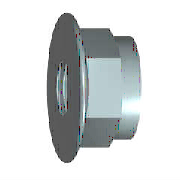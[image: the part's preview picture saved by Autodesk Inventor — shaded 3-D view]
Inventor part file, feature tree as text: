
AUTODESK INVENTOR PART (.ipt)
format: ipt  version: 2018 (Build 220112000, 112)  size: 212,480 bytes
history: native  units: mm (DEFAULTED — no unit token found)
features: other x3, sketch x3, extrude x2, hole x1, plane x1
ambient origin geometry x7: Origin, YZ Plane, XZ Plane, X Axis, Y Axis, Z Axis, Center Point
bodies: Solid1 (feature_tree)
feature tree (10):
  other  "Anello"
  extrude  "Corpo"  Depth=34.5mm
  extrude  "Corona"  Depth=2.4mm
  hole  "Filettatura"  [1 undecoded]
  other  "Smusso1"
  other  "Work Axis1"
  plane  "Work Plane1"
  sketch  "Schizzo1"
  sketch  "Schizzo5"
  sketch  "Schizzo3"
note: 1 required parameter value undecoded (feature->parameter linkage not recoverable at this tier; creation-order binding heuristic only, values carry confidence <= 0.55)
